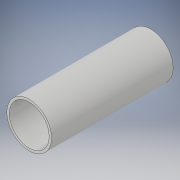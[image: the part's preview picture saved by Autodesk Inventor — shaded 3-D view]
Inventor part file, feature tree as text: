
AUTODESK INVENTOR PART (.ipt)
format: ipt  version: 2019 (Build 230136000, 136)  size: 98,816 bytes
history: native  units: mm
features: extrude x2, sketch x2
ambient origin geometry x8: Origin, YZ Plane, XZ Plane, XY Plane, X Axis, Y Axis, Z Axis, Center Point
bodies: Solid1 (feature_tree)
feature tree (4):
  extrude  "Extrusion1"  Depth=540.0mm TaperAngle=0.0deg
  extrude  "Extrusion2"  Depth=54.0mm TaperAngle=0.0deg
  sketch  "Sketch1"  dims[d0=198.7mm d1=540.0mm d2=0.0mm]
  sketch  "Sketch2"  dims[d3=177.2mm d4=54.0mm d5=0.0mm]
